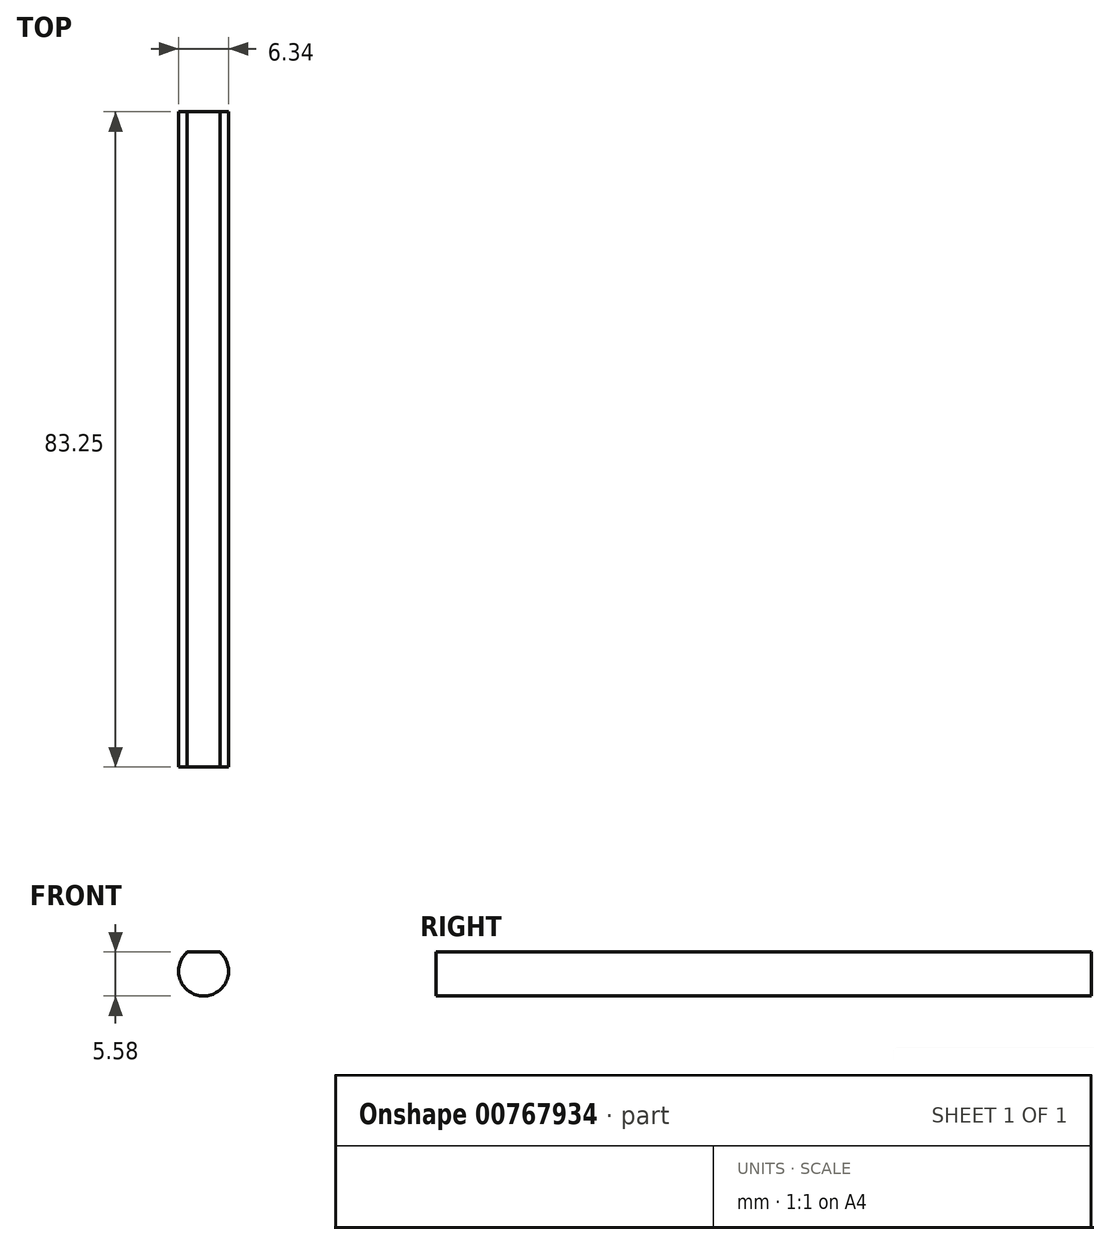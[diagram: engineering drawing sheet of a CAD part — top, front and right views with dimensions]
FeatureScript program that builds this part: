
annotation { "Feature Type Name" : "Feature", "Feature Type Description" : "" }
export const myFeature = defineFeature(function(context is Context, id is Id, definition is map)
    precondition{}
    {
        {
            var Q0;
            Q0=qCreatedBy(makeId("Front.planeOp"),FACE);
            var sketch = newSketch(context, id + "F0", { "sketchPlane" : qUnion([Q0])});
            skArc(sketch, "E0", {"start": v(-2.07, 2.41) * mm, "mid": v(0, -3.17) * mm, "end": v(2.07, 2.41) * mm});
            skLineSegment(sketch, "E1", {"start": v(2.07, 2.41) * mm, "end": v(-2.07, 2.41) * mm});
            skSolve(sketch);
        }
        {
            var Q0;
            Q0=makeQuery(id+"F0.imprint","IMPRINT",FACE,{"disambiguationData":[TD([[makeQuery(id+"F0.imprint","IMPRINT",EDGE,{"derivedFrom":sQuery(id+"F0.wireOp",EDGE,"E0")}),1.0]])]});
            extrude(context, id + "F1", {"entities" : qUnion([Q0]), "depth" : (61 + 22.25) * mm, "offsetDistance" : 25 * mm});
        }
    });
